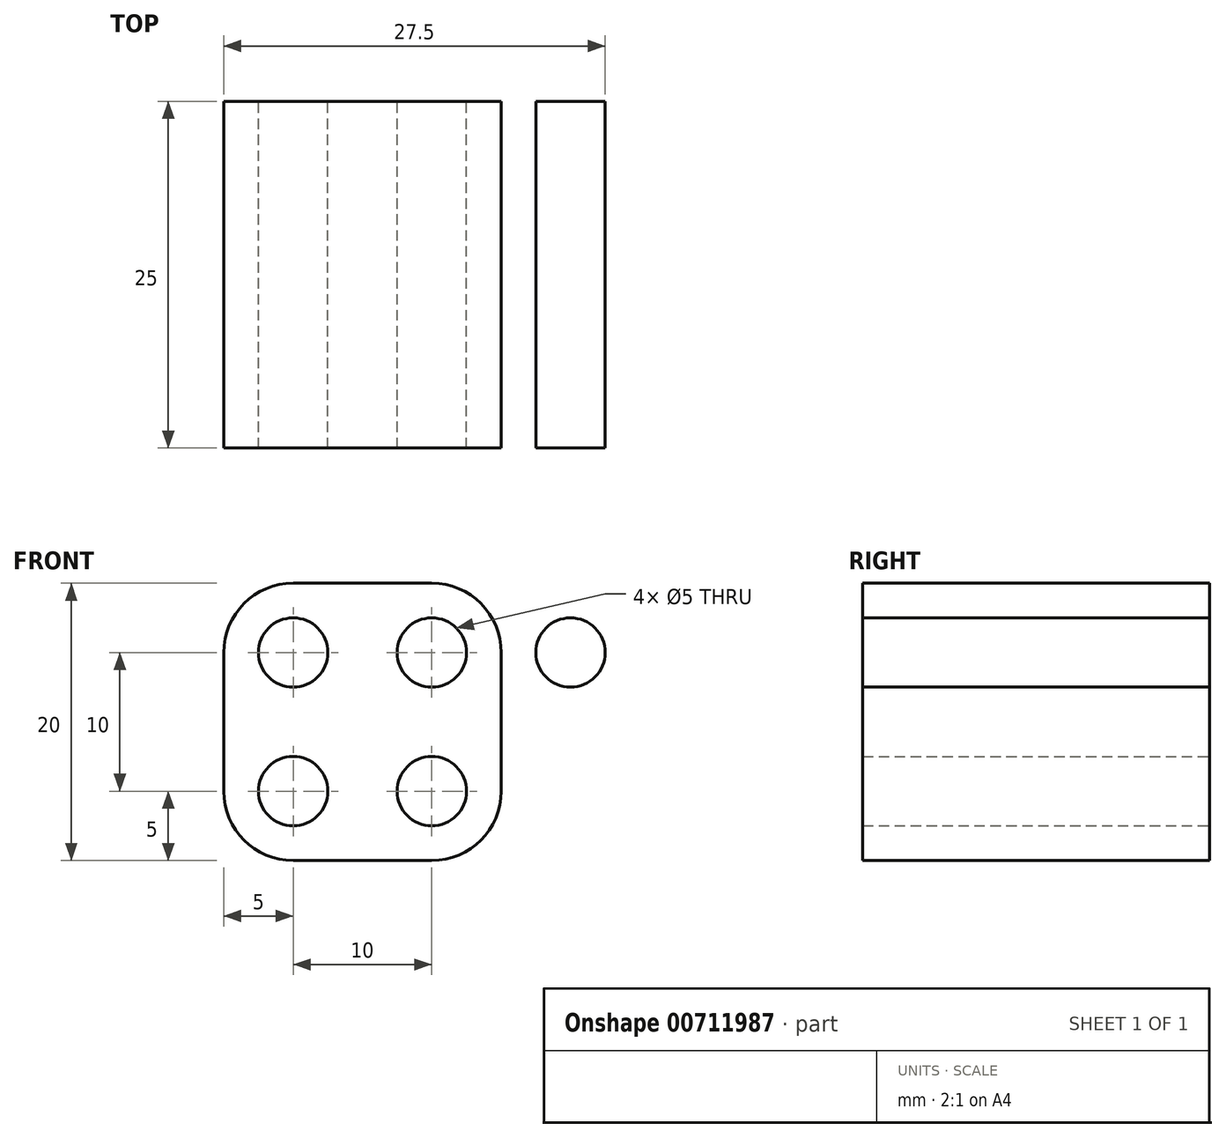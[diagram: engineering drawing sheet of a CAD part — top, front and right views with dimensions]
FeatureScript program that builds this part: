
annotation { "Feature Type Name" : "Feature", "Feature Type Description" : "" }
export const myFeature = defineFeature(function(context is Context, id is Id, definition is map)
    precondition{}
    {
        {
            var Q0;
            Q0=qCreatedBy(makeId("Front.planeOp"),FACE);
            var sketch = newSketch(context, id + "F0", { "sketchPlane" : qUnion([Q0])});
            skLineSegment(sketch, "E0.bottom", {"start": v(-5, 10) * mm, "end": v(5, 10) * mm});
            skLineSegment(sketch, "E0.top", {"start": v(-5, -10) * mm, "end": v(5, -10) * mm});
            skLineSegment(sketch, "E0.left", {"start": v(-10, 5) * mm, "end": v(-10, -5) * mm});
            skLineSegment(sketch, "E0.right", {"start": v(10, 5) * mm, "end": v(10, -5) * mm});
            skPoint(sketch, "E0.middle", {"position": v(0, 0) * mm});
            skPoint(sketch, "E1.visualSharp", {"position": v(-10, 10) * mm});
            skArc(sketch, "E1.filletArc", {"start": v(-5, 10) * mm, "mid": v(-8.54, 8.54) * mm, "end": v(-10, 5) * mm});
            skPoint(sketch, "E2.visualSharp", {"position": v(10, 10) * mm});
            skArc(sketch, "E2.filletArc", {"start": v(10, 5) * mm, "mid": v(8.54, 8.54) * mm, "end": v(5, 10) * mm});
            skPoint(sketch, "E3.visualSharp", {"position": v(10, -10) * mm});
            skArc(sketch, "E3.filletArc", {"start": v(5, -10) * mm, "mid": v(8.54, -8.54) * mm, "end": v(10, -5) * mm});
            skPoint(sketch, "E4.visualSharp", {"position": v(-10, -10) * mm});
            skArc(sketch, "E4.filletArc", {"start": v(-10, -5) * mm, "mid": v(-8.54, -8.54) * mm, "end": v(-5, -10) * mm});
            skCircle(sketch, "E5", {"center": v(-5, 5) * mm, "radius": 2.5 * mm});
            skCircle(sketch, "E6.1.0.0", {"center": v(5, 5) * mm, "radius": 2.5 * mm});
            skLineSegment(sketch, "E6.direction1", {"start": v(-5, 5) * mm, "end": v(5, 5) * mm, "construction": true});
            skLineSegment(sketch, "E7", {"start": v(-10, 0) * mm, "end": v(10, 0) * mm, "construction": true});
            skCircle(sketch, "E8.MirrorC", {"center": v(5, -5) * mm, "radius": 2.5 * mm});
            skCircle(sketch, "E9.MirrorC", {"center": v(-5, -5) * mm, "radius": 2.5 * mm});
            skCircle(sketch, "E10.0.2.0", {"center": v(15, 5) * mm, "radius": 2.5 * mm});
            skSolve(sketch);
        }
        {
            var Q0;
            Q0 = qSketchRegion(id + "F0", true);
            extrude(context, id + "F1", {"entities" : qUnion([Q0]), "depth" : 25 * mm, "offsetDistance" : 25 * mm});
        }
    });
